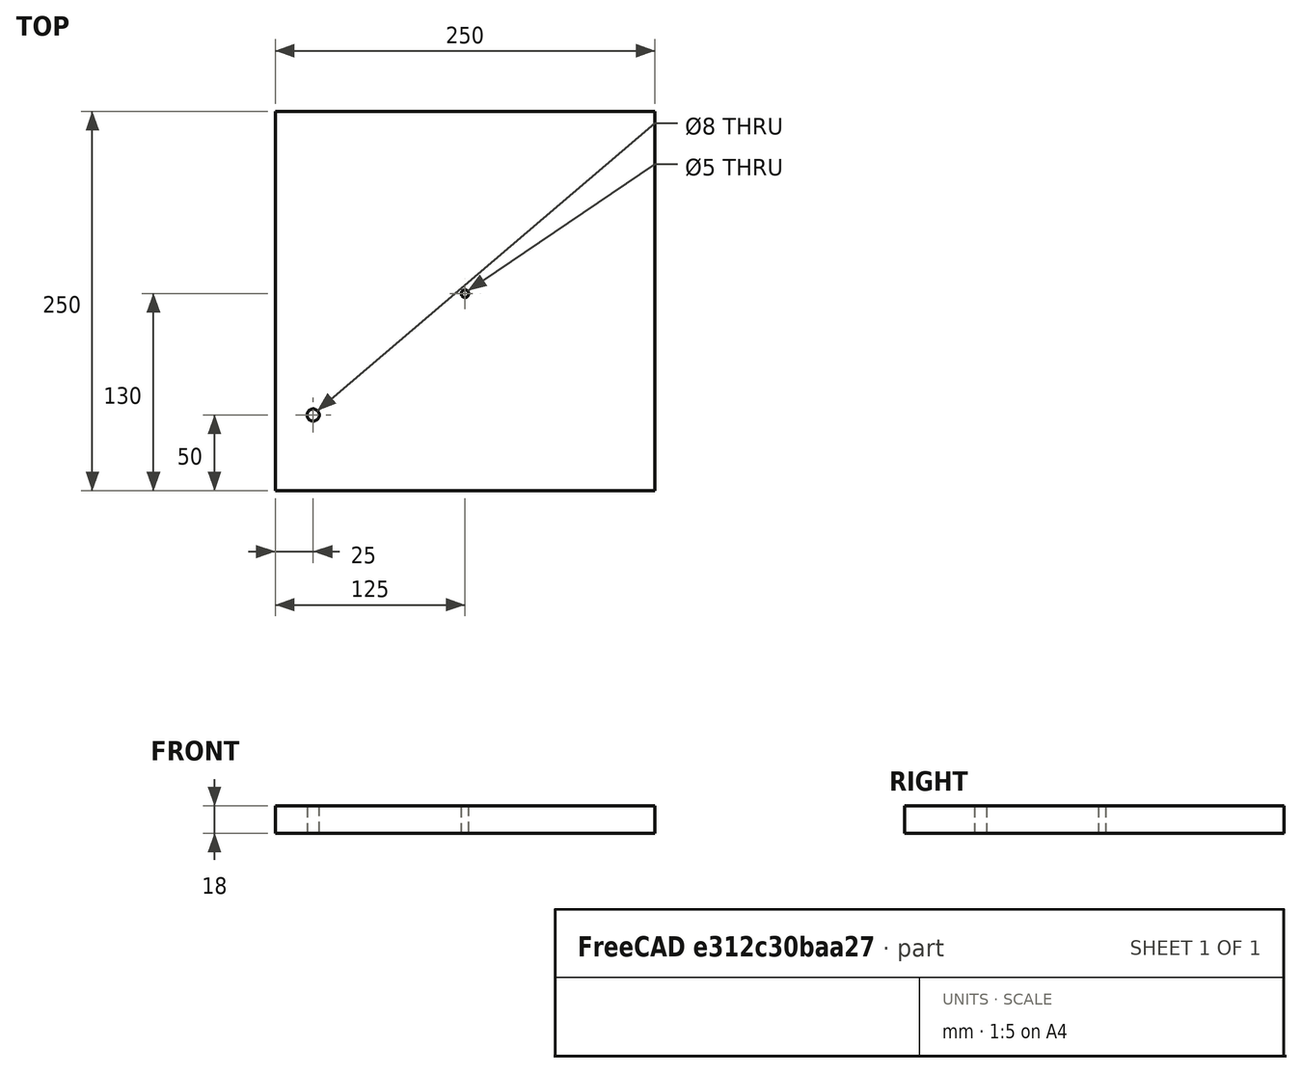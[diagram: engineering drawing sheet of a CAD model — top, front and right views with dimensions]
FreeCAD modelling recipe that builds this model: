
FCSTD DOCUMENT  (FreeCAD 0.22R35176 (Git))
Label: knob_jig
License: All rights reserved
LicenseURL: http://en.wikipedia.org/wiki/All_rights_reserved
objects: Sketcher::SketchObject×1, PartDesign::Pad×1, PartDesign::Body×1
note: 4 computed .brp shape members not serialized (recipe doc carries the construction recipe); baked Part::Feature solids carry a one-line shape summary decoded from their .brp

FEATURE [Sketcher::SketchObject] Sketch
  FullyConstrained = true
  MapMode = 5
  Support = -> [XY_Plane]
  expr: Constraints[16] = 100
  sketch-geometry (7):
    g0: LineSegment StartX=-125 StartY=250 StartZ=0 EndX=-125 EndY=0 EndZ=0
    g1: LineSegment StartX=-125 StartY=0 StartZ=0 EndX=125 EndY=0 EndZ=0
    g2: LineSegment StartX=125 StartY=0 StartZ=0 EndX=125 EndY=250 EndZ=0
    g3: LineSegment StartX=125 StartY=250 StartZ=0 EndX=-125 EndY=250 EndZ=0
    g4: Circle CenterX=0 CenterY=130 CenterZ=0 NormalX=0 NormalY=0 NormalZ=1 AngleXU=0 Radius=2.5
    g5: Circle CenterX=0 CenterY=130 CenterZ=0 NormalX=0 NormalY=0 NormalZ=1 AngleXU=0 Radius=50
    g6: Circle CenterX=-100 CenterY=50 CenterZ=0 NormalX=0 NormalY=0 NormalZ=1 AngleXU=0 Radius=4
  constraints (19):
    c: Coincident(g0,g1)
    c: Coincident(g1,g2)
    c: Coincident(g2,g3)
    c: Coincident(g3,g0)
    c: Vertical(g0)
    c: Vertical(g2)
    c: Horizontal(g1)
    c: Horizontal(g3)
    c: Symmetric(g0,g1,g-1)
    c: Equal(g0,g3)
    c: DistanceX(g1,g1) = 250
    c: PointOnObject(g4,g-2)
    c: Diameter(g4) = 5
    c: DistanceY(g-1,g4) = 130
    c: Coincident(g5,g4)
    c: Diameter(g5) = 100
    c: DistanceX(g6,g-1) = 100
    c: DistanceY(g-1,g6) = 50
    c: Diameter(g6) = 8
FEATURE [PartDesign::Pad] Pad
  Direction = (0,0,1)
  Length = 18
  Length2 = 10
  Profile = -> Sketch
  ReferenceAxis = -> Sketch [N_Axis]
  Type = 0
FEATURE [PartDesign::Body] Body
  Group = -> [Sketch,Pad]
  Origin = -> Origin
  Tip = -> Pad
